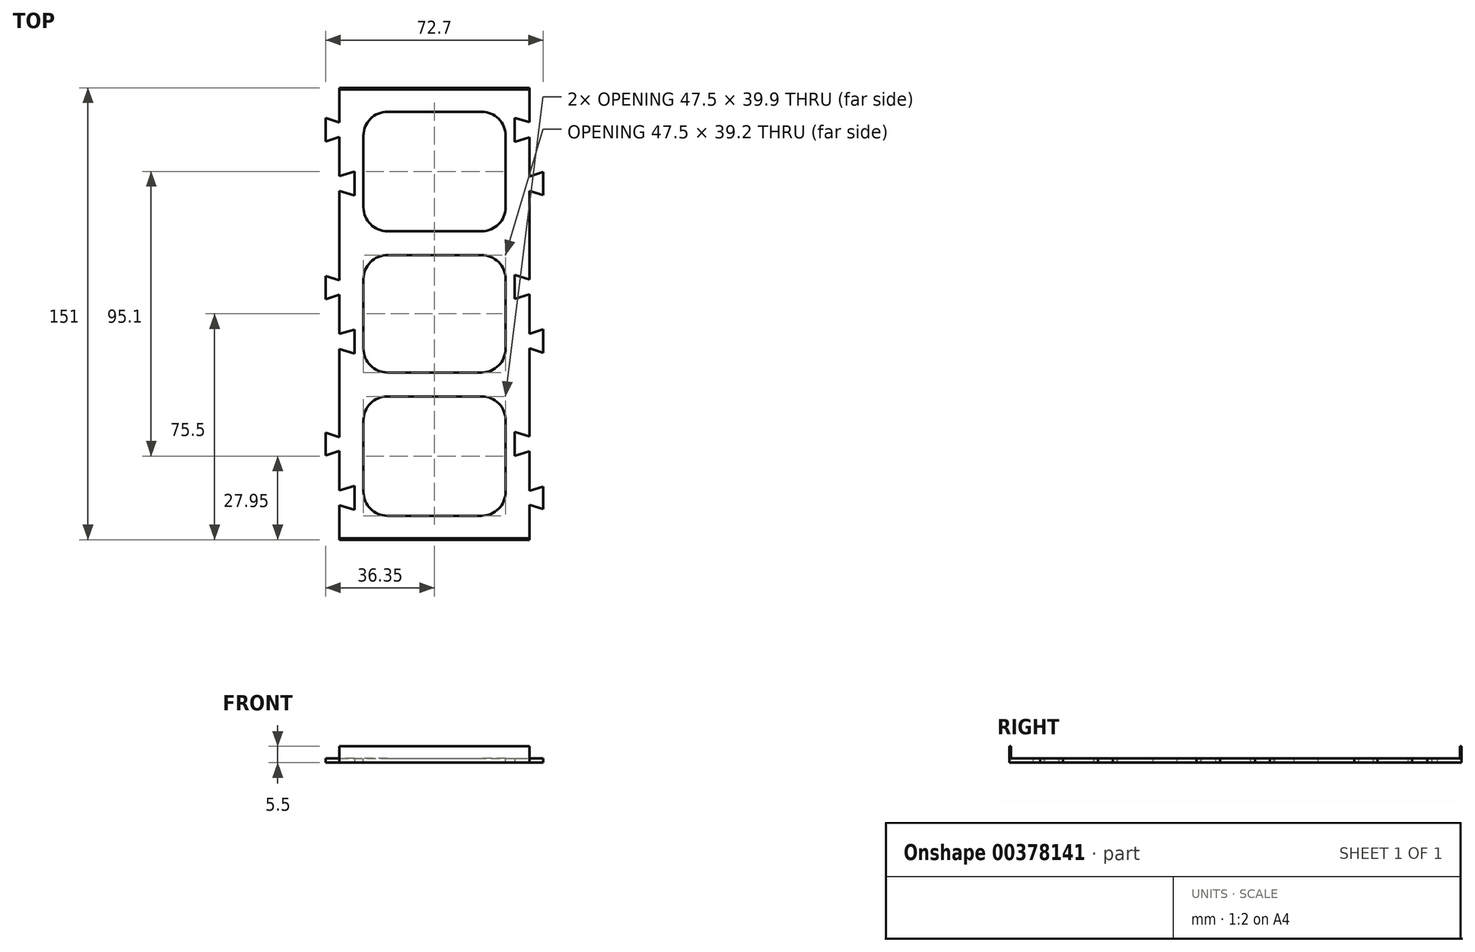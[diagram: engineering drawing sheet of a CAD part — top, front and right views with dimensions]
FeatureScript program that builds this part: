
annotation { "Feature Type Name" : "Feature", "Feature Type Description" : "" }
export const myFeature = defineFeature(function(context is Context, id is Id, definition is map)
    precondition{}
    {
        {
            var Q0;
            Q0=qCreatedBy(makeId("Top.planeOp"),FACE);
            var sketch = newSketch(context, id + "F0", { "sketchPlane" : qUnion([Q0])});
            skLineSegment(sketch, "E0", {"start": v(0, 0) * mm, "end": v(0, 11.5) * mm});
            skLineSegment(sketch, "E1", {"start": v(0, 11.5) * mm, "end": v(5, 10) * mm});
            skLineSegment(sketch, "E2", {"start": v(5, 10) * mm, "end": v(5, 18) * mm});
            skLineSegment(sketch, "E3", {"start": v(5, 18) * mm, "end": v(0, 16.5) * mm});
            skLineSegment(sketch, "E4", {"start": v(0, 16.5) * mm, "end": v(0, 29.7) * mm});
            skLineSegment(sketch, "E5", {"start": v(0, 29.7) * mm, "end": v(-4.6, 28.2) * mm});
            skLineSegment(sketch, "E6", {"start": v(-4.6, 28.2) * mm, "end": v(-4.6, 35.8) * mm});
            skLineSegment(sketch, "E7", {"start": v(-4.6, 35.8) * mm, "end": v(0, 34.3) * mm});
            skLineSegment(sketch, "E8", {"start": v(0, 34.3) * mm, "end": v(0, 63.75) * mm});
            skLineSegment(sketch, "E9", {"start": v(0, 63.75) * mm, "end": v(5, 62.25) * mm});
            skLineSegment(sketch, "E10", {"start": v(5, 62.25) * mm, "end": v(5, 70.25) * mm});
            skLineSegment(sketch, "E11", {"start": v(5, 70.25) * mm, "end": v(0, 68.75) * mm});
            skLineSegment(sketch, "E12", {"start": v(0, 68.75) * mm, "end": v(0, 81.85) * mm});
            skLineSegment(sketch, "E13", {"start": v(0, 81.85) * mm, "end": v(-4.6, 80.35) * mm});
            skLineSegment(sketch, "E14", {"start": v(-4.6, 80.35) * mm, "end": v(-4.6, 88.15) * mm});
            skLineSegment(sketch, "E15", {"start": v(-4.6, 88.15) * mm, "end": v(0, 86.65) * mm});
            skLineSegment(sketch, "E16", {"start": v(0, 86.65) * mm, "end": v(0, 116.5) * mm});
            skLineSegment(sketch, "E17", {"start": v(0, 116.5) * mm, "end": v(5, 115) * mm});
            skLineSegment(sketch, "E18", {"start": v(5, 115) * mm, "end": v(5, 123) * mm});
            skLineSegment(sketch, "E19", {"start": v(5, 123) * mm, "end": v(0, 121.5) * mm});
            skLineSegment(sketch, "E20", {"start": v(0, 121.5) * mm, "end": v(0, 134.6) * mm});
            skLineSegment(sketch, "E21", {"start": v(0, 134.6) * mm, "end": v(-4.6, 133.1) * mm});
            skLineSegment(sketch, "E22", {"start": v(-4.6, 133.1) * mm, "end": v(-4.6, 140.9) * mm});
            skLineSegment(sketch, "E23", {"start": v(-4.6, 140.9) * mm, "end": v(0, 139.4) * mm});
            skLineSegment(sketch, "E24", {"start": v(0, 139.4) * mm, "end": v(0, 151) * mm});
            skLineSegment(sketch, "E25", {"start": v(0, 151) * mm, "end": v(63.5, 151) * mm});
            skLineSegment(sketch, "E26", {"start": v(63.5, 151) * mm, "end": v(63.5, 139.5) * mm});
            skLineSegment(sketch, "E27", {"start": v(63.5, 139.5) * mm, "end": v(58.5, 141) * mm});
            skLineSegment(sketch, "E28", {"start": v(58.5, 141) * mm, "end": v(58.5, 133) * mm});
            skLineSegment(sketch, "E29", {"start": v(58.5, 133) * mm, "end": v(63.5, 134.5) * mm});
            skLineSegment(sketch, "E30", {"start": v(63.5, 134.5) * mm, "end": v(63.5, 121.4) * mm});
            skLineSegment(sketch, "E31", {"start": v(63.5, 121.4) * mm, "end": v(68.1, 122.9) * mm});
            skLineSegment(sketch, "E32", {"start": v(68.1, 122.9) * mm, "end": v(68.1, 115.1) * mm});
            skLineSegment(sketch, "E33", {"start": v(68.1, 115.1) * mm, "end": v(63.5, 116.6) * mm});
            skLineSegment(sketch, "E34", {"start": v(63.5, 116.6) * mm, "end": v(63.5, 87) * mm});
            skLineSegment(sketch, "E35", {"start": v(63.5, 87) * mm, "end": v(58.5, 88.5) * mm});
            skLineSegment(sketch, "E36", {"start": v(58.5, 88.5) * mm, "end": v(58.5, 80.5) * mm});
            skLineSegment(sketch, "E37", {"start": v(58.5, 80.5) * mm, "end": v(63.5, 82) * mm});
            skLineSegment(sketch, "E38", {"start": v(63.5, 82) * mm, "end": v(63.5, 68.8) * mm});
            skLineSegment(sketch, "E39", {"start": v(63.5, 68.8) * mm, "end": v(68.1, 70.3) * mm});
            skLineSegment(sketch, "E40", {"start": v(68.1, 70.3) * mm, "end": v(68.1, 62.5) * mm});
            skLineSegment(sketch, "E41", {"start": v(68.1, 62.5) * mm, "end": v(63.5, 64) * mm});
            skLineSegment(sketch, "E42", {"start": v(63.5, 64) * mm, "end": v(63.5, 34.5) * mm});
            skLineSegment(sketch, "E43", {"start": v(63.5, 34.5) * mm, "end": v(58.5, 36) * mm});
            skLineSegment(sketch, "E44", {"start": v(58.5, 36) * mm, "end": v(58.5, 28) * mm});
            skLineSegment(sketch, "E45", {"start": v(58.5, 28) * mm, "end": v(63.5, 29.5) * mm});
            skLineSegment(sketch, "E46", {"start": v(63.5, 29.5) * mm, "end": v(63.5, 16.3) * mm});
            skLineSegment(sketch, "E47", {"start": v(63.5, 16.3) * mm, "end": v(68.1, 17.8) * mm});
            skLineSegment(sketch, "E48", {"start": v(68.1, 17.8) * mm, "end": v(68.1, 10.2) * mm});
            skLineSegment(sketch, "E49", {"start": v(68.1, 10.2) * mm, "end": v(63.5, 11.7) * mm});
            skLineSegment(sketch, "E50", {"start": v(63.5, 11.7) * mm, "end": v(63.5, 0) * mm});
            skLineSegment(sketch, "E51", {"start": v(63.5, 0) * mm, "end": v(0, 0) * mm});
            skSolve(sketch);
        }
        {
            var Q0;
            Q0=makeQuery(id+"F0.imprint","IMPRINT",FACE,{"disambiguationData":[TD([[makeQuery(id+"F0.imprint","IMPRINT",EDGE,{"derivedFrom":sQuery(id+"F0.wireOp",EDGE,"E0")}),-1.0]])]});
            extrude(context, id + "F1", {"entities" : qUnion([Q0]), "depth" : 1.5 * mm});
        }
        {
            var Q0;
            Q0=makeQuery(id+"F1.opExtrude","CAP_FACE",FACE,{"disambiguationData":[OSD([sQuery(id+"F0.wireOp",EDGE,"E0"),sQuery(id+"F0.wireOp",EDGE,"E1"),sQuery(id+"F0.wireOp",EDGE,"E2"),sQuery(id+"F0.wireOp",EDGE,"E3"),sQuery(id+"F0.wireOp",EDGE,"E4"),sQuery(id+"F0.wireOp",EDGE,"E5"),sQuery(id+"F0.wireOp",EDGE,"E6"),sQuery(id+"F0.wireOp",EDGE,"E7"),sQuery(id+"F0.wireOp",EDGE,"E8"),sQuery(id+"F0.wireOp",EDGE,"E9"),sQuery(id+"F0.wireOp",EDGE,"E10"),sQuery(id+"F0.wireOp",EDGE,"E11"),sQuery(id+"F0.wireOp",EDGE,"E12"),sQuery(id+"F0.wireOp",EDGE,"E13"),sQuery(id+"F0.wireOp",EDGE,"E14"),sQuery(id+"F0.wireOp",EDGE,"E15"),sQuery(id+"F0.wireOp",EDGE,"E16"),sQuery(id+"F0.wireOp",EDGE,"E17"),sQuery(id+"F0.wireOp",EDGE,"E18"),sQuery(id+"F0.wireOp",EDGE,"E19"),sQuery(id+"F0.wireOp",EDGE,"E20"),sQuery(id+"F0.wireOp",EDGE,"E21"),sQuery(id+"F0.wireOp",EDGE,"E22"),sQuery(id+"F0.wireOp",EDGE,"E23"),sQuery(id+"F0.wireOp",EDGE,"E24"),sQuery(id+"F0.wireOp",EDGE,"E25"),sQuery(id+"F0.wireOp",EDGE,"E26"),sQuery(id+"F0.wireOp",EDGE,"E27"),sQuery(id+"F0.wireOp",EDGE,"E28"),sQuery(id+"F0.wireOp",EDGE,"E29"),sQuery(id+"F0.wireOp",EDGE,"E30"),sQuery(id+"F0.wireOp",EDGE,"E31"),sQuery(id+"F0.wireOp",EDGE,"E32"),sQuery(id+"F0.wireOp",EDGE,"E33"),sQuery(id+"F0.wireOp",EDGE,"E34"),sQuery(id+"F0.wireOp",EDGE,"E35"),sQuery(id+"F0.wireOp",EDGE,"E36"),sQuery(id+"F0.wireOp",EDGE,"E37"),sQuery(id+"F0.wireOp",EDGE,"E38"),sQuery(id+"F0.wireOp",EDGE,"E39"),sQuery(id+"F0.wireOp",EDGE,"E40"),sQuery(id+"F0.wireOp",EDGE,"E41"),sQuery(id+"F0.wireOp",EDGE,"E42"),sQuery(id+"F0.wireOp",EDGE,"E43"),sQuery(id+"F0.wireOp",EDGE,"E44"),sQuery(id+"F0.wireOp",EDGE,"E45"),sQuery(id+"F0.wireOp",EDGE,"E46"),sQuery(id+"F0.wireOp",EDGE,"E47"),sQuery(id+"F0.wireOp",EDGE,"E48"),sQuery(id+"F0.wireOp",EDGE,"E49"),sQuery(id+"F0.wireOp",EDGE,"E50"),sQuery(id+"F0.wireOp",EDGE,"E51")])],"isStart":false});
            var sketch = newSketch(context, id + "F2", { "sketchPlane" : qUnion([Q0])});
            skLineSegment(sketch, "E52.bottom", {"start": v(0, 151) * mm, "end": v(63.5, 151) * mm});
            skLineSegment(sketch, "E52.top", {"start": v(0, 150.5) * mm, "end": v(63.5, 150.5) * mm});
            skLineSegment(sketch, "E52.left", {"start": v(0, 151) * mm, "end": v(0, 150.5) * mm});
            skLineSegment(sketch, "E52.right", {"start": v(63.5, 151) * mm, "end": v(63.5, 150.5) * mm});
            skLineSegment(sketch, "E53.bottom", {"start": v(0, 0) * mm, "end": v(75.6, 0) * mm});
            skLineSegment(sketch, "E53.top", {"start": v(0, 0.5) * mm, "end": v(75.6, 0.5) * mm});
            skLineSegment(sketch, "E53.left", {"start": v(0, 0) * mm, "end": v(0, 0.5) * mm});
            skLineSegment(sketch, "E53.right", {"start": v(75.6, 0) * mm, "end": v(75.6, 0.5) * mm});
            skSolve(sketch);
        }
        {
            var Q0;
            Q0=makeQuery(id+"F2.imprint","IMPRINT",FACE,{"disambiguationData":[TD([[makeQuery(id+"F2.imprint","IMPRINT",EDGE,{"derivedFrom":sQuery(id+"F2.wireOp",EDGE,"E53.bottom")}),-1.0]])]});
            var Q1;
            Q1=makeQuery(id+"F2.imprint","IMPRINT",FACE,{"disambiguationData":[TD([[makeQuery(id+"F2.imprint","IMPRINT",EDGE,{"derivedFrom":sQuery(id+"F2.wireOp",EDGE,"E52.bottom")}),-1.0]])]});
            extrude(context, id + "F3", {"entities" : qUnion([Q0, Q1]), "operationType" : NewBodyOperationType.ADD, "depth" : 4 * mm});
        }
        {
            var Q0;
            Q0=makeQuery(id+"F1.opExtrude","CAP_FACE",FACE,{"disambiguationData":[OSD([sQuery(id+"F0.wireOp",EDGE,"E0"),sQuery(id+"F0.wireOp",EDGE,"E1"),sQuery(id+"F0.wireOp",EDGE,"E2"),sQuery(id+"F0.wireOp",EDGE,"E3"),sQuery(id+"F0.wireOp",EDGE,"E4"),sQuery(id+"F0.wireOp",EDGE,"E5"),sQuery(id+"F0.wireOp",EDGE,"E6"),sQuery(id+"F0.wireOp",EDGE,"E7"),sQuery(id+"F0.wireOp",EDGE,"E8"),sQuery(id+"F0.wireOp",EDGE,"E9"),sQuery(id+"F0.wireOp",EDGE,"E10"),sQuery(id+"F0.wireOp",EDGE,"E11"),sQuery(id+"F0.wireOp",EDGE,"E12"),sQuery(id+"F0.wireOp",EDGE,"E13"),sQuery(id+"F0.wireOp",EDGE,"E14"),sQuery(id+"F0.wireOp",EDGE,"E15"),sQuery(id+"F0.wireOp",EDGE,"E16"),sQuery(id+"F0.wireOp",EDGE,"E17"),sQuery(id+"F0.wireOp",EDGE,"E18"),sQuery(id+"F0.wireOp",EDGE,"E19"),sQuery(id+"F0.wireOp",EDGE,"E20"),sQuery(id+"F0.wireOp",EDGE,"E21"),sQuery(id+"F0.wireOp",EDGE,"E22"),sQuery(id+"F0.wireOp",EDGE,"E23"),sQuery(id+"F0.wireOp",EDGE,"E24"),sQuery(id+"F0.wireOp",EDGE,"E25"),sQuery(id+"F0.wireOp",EDGE,"E26"),sQuery(id+"F0.wireOp",EDGE,"E27"),sQuery(id+"F0.wireOp",EDGE,"E28"),sQuery(id+"F0.wireOp",EDGE,"E29"),sQuery(id+"F0.wireOp",EDGE,"E30"),sQuery(id+"F0.wireOp",EDGE,"E31"),sQuery(id+"F0.wireOp",EDGE,"E32"),sQuery(id+"F0.wireOp",EDGE,"E33"),sQuery(id+"F0.wireOp",EDGE,"E34"),sQuery(id+"F0.wireOp",EDGE,"E35"),sQuery(id+"F0.wireOp",EDGE,"E36"),sQuery(id+"F0.wireOp",EDGE,"E37"),sQuery(id+"F0.wireOp",EDGE,"E38"),sQuery(id+"F0.wireOp",EDGE,"E39"),sQuery(id+"F0.wireOp",EDGE,"E40"),sQuery(id+"F0.wireOp",EDGE,"E41"),sQuery(id+"F0.wireOp",EDGE,"E42"),sQuery(id+"F0.wireOp",EDGE,"E43"),sQuery(id+"F0.wireOp",EDGE,"E44"),sQuery(id+"F0.wireOp",EDGE,"E45"),sQuery(id+"F0.wireOp",EDGE,"E46"),sQuery(id+"F0.wireOp",EDGE,"E47"),sQuery(id+"F0.wireOp",EDGE,"E48"),sQuery(id+"F0.wireOp",EDGE,"E49"),sQuery(id+"F0.wireOp",EDGE,"E50"),sQuery(id+"F0.wireOp",EDGE,"E51")])],"isStart":false});
            var sketch = newSketch(context, id + "F4", { "sketchPlane" : qUnion([Q0])});
            skLineSegment(sketch, "E54.bottom", {"start": v(8, 47.9) * mm, "end": v(55.5, 47.9) * mm});
            skLineSegment(sketch, "E54.top", {"start": v(8, 8) * mm, "end": v(55.5, 8) * mm});
            skLineSegment(sketch, "E54.left", {"start": v(8, 47.9) * mm, "end": v(8, 8) * mm});
            skLineSegment(sketch, "E54.right", {"start": v(55.5, 47.9) * mm, "end": v(55.5, 8) * mm});
            skLineSegment(sketch, "E55.bottom", {"start": v(8, 95.1) * mm, "end": v(55.5, 95.1) * mm});
            skLineSegment(sketch, "E55.top", {"start": v(8, 55.9) * mm, "end": v(55.5, 55.9) * mm});
            skLineSegment(sketch, "E55.left", {"start": v(8, 95.1) * mm, "end": v(8, 55.9) * mm});
            skLineSegment(sketch, "E55.right", {"start": v(55.5, 95.1) * mm, "end": v(55.5, 55.9) * mm});
            skLineSegment(sketch, "E56.bottom", {"start": v(8, 143) * mm, "end": v(55.5, 143) * mm});
            skLineSegment(sketch, "E56.top", {"start": v(8, 103.1) * mm, "end": v(55.5, 103.1) * mm});
            skLineSegment(sketch, "E56.left", {"start": v(8, 143) * mm, "end": v(8, 103.1) * mm});
            skLineSegment(sketch, "E56.right", {"start": v(55.5, 143) * mm, "end": v(55.5, 103.1) * mm});
            skSolve(sketch);
        }
        {
            var Q0;
            Q0=makeQuery(id+"F4.imprint","IMPRINT",FACE,{"disambiguationData":[TD([[makeQuery(id+"F4.imprint","IMPRINT",EDGE,{"derivedFrom":sQuery(id+"F4.wireOp",EDGE,"E56.bottom")}),-1.0]])]});
            var Q1;
            Q1=makeQuery(id+"F4.imprint","IMPRINT",FACE,{"disambiguationData":[TD([[makeQuery(id+"F4.imprint","IMPRINT",EDGE,{"derivedFrom":sQuery(id+"F4.wireOp",EDGE,"E55.bottom")}),-1.0]])]});
            var Q2;
            Q2=makeQuery(id+"F4.imprint","IMPRINT",FACE,{"disambiguationData":[TD([[makeQuery(id+"F4.imprint","IMPRINT",EDGE,{"derivedFrom":sQuery(id+"F4.wireOp",EDGE,"E54.bottom")}),-1.0]])]});
            extrude(context, id + "F5", {"entities" : qUnion([Q0, Q1, Q2]), "operationType" : NewBodyOperationType.REMOVE, "endBound" : BoundingType.THROUGH_ALL, "oppositeDirection" : true, "depth" : 25 * mm});
        }
        {
            var Q0;
            Q0=makeQuery(id+"F5.boolean.opBoolean","COPY",EDGE,{"derivedFrom":makeQuery(id+"F5.opExtrude","SWEPT_EDGE",EDGE,{"disambiguationData":[OSD([sQuery(id+"F4.wireOp",EDGE,"E56.bottom"),sQuery(id+"F4.wireOp",EDGE,"E56.left")])]})});
            var Q1;
            Q1=makeQuery(id+"F5.boolean.opBoolean","COPY",EDGE,{"derivedFrom":makeQuery(id+"F5.opExtrude","SWEPT_EDGE",EDGE,{"disambiguationData":[OSD([sQuery(id+"F4.wireOp",EDGE,"E55.bottom"),sQuery(id+"F4.wireOp",EDGE,"E55.left")])]})});
            var Q2;
            Q2=makeQuery(id+"F5.boolean.opBoolean","COPY",EDGE,{"derivedFrom":makeQuery(id+"F5.opExtrude","SWEPT_EDGE",EDGE,{"disambiguationData":[OSD([sQuery(id+"F4.wireOp",EDGE,"E54.bottom"),sQuery(id+"F4.wireOp",EDGE,"E54.left")])]})});
            var Q3;
            Q3=makeQuery(id+"F5.boolean.opBoolean","COPY",EDGE,{"derivedFrom":makeQuery(id+"F5.opExtrude","SWEPT_EDGE",EDGE,{"disambiguationData":[OSD([sQuery(id+"F4.wireOp",EDGE,"E56.top"),sQuery(id+"F4.wireOp",EDGE,"E56.left")])]})});
            var Q4;
            Q4=makeQuery(id+"F5.boolean.opBoolean","COPY",EDGE,{"derivedFrom":makeQuery(id+"F5.opExtrude","SWEPT_EDGE",EDGE,{"disambiguationData":[OSD([sQuery(id+"F4.wireOp",EDGE,"E55.top"),sQuery(id+"F4.wireOp",EDGE,"E55.left")])]})});
            var Q5;
            Q5=makeQuery(id+"F5.boolean.opBoolean","COPY",EDGE,{"derivedFrom":makeQuery(id+"F5.opExtrude","SWEPT_EDGE",EDGE,{"disambiguationData":[OSD([sQuery(id+"F4.wireOp",EDGE,"E54.top"),sQuery(id+"F4.wireOp",EDGE,"E54.left")])]})});
            var Q6;
            Q6=makeQuery(id+"F5.boolean.opBoolean","COPY",EDGE,{"derivedFrom":makeQuery(id+"F5.opExtrude","SWEPT_EDGE",EDGE,{"disambiguationData":[OSD([sQuery(id+"F4.wireOp",EDGE,"E54.top"),sQuery(id+"F4.wireOp",EDGE,"E54.right")])]})});
            var Q7;
            Q7=makeQuery(id+"F5.boolean.opBoolean","COPY",EDGE,{"derivedFrom":makeQuery(id+"F5.opExtrude","SWEPT_EDGE",EDGE,{"disambiguationData":[OSD([sQuery(id+"F4.wireOp",EDGE,"E55.top"),sQuery(id+"F4.wireOp",EDGE,"E55.right")])]})});
            var Q8;
            Q8=makeQuery(id+"F5.boolean.opBoolean","COPY",EDGE,{"derivedFrom":makeQuery(id+"F5.opExtrude","SWEPT_EDGE",EDGE,{"disambiguationData":[OSD([sQuery(id+"F4.wireOp",EDGE,"E56.top"),sQuery(id+"F4.wireOp",EDGE,"E56.right")])]})});
            var Q9;
            Q9=makeQuery(id+"F5.boolean.opBoolean","COPY",EDGE,{"derivedFrom":makeQuery(id+"F5.opExtrude","SWEPT_EDGE",EDGE,{"disambiguationData":[OSD([sQuery(id+"F4.wireOp",EDGE,"E56.bottom"),sQuery(id+"F4.wireOp",EDGE,"E56.right")])]})});
            var Q10;
            Q10=makeQuery(id+"F5.boolean.opBoolean","COPY",EDGE,{"derivedFrom":makeQuery(id+"F5.opExtrude","SWEPT_EDGE",EDGE,{"disambiguationData":[OSD([sQuery(id+"F4.wireOp",EDGE,"E55.bottom"),sQuery(id+"F4.wireOp",EDGE,"E55.right")])]})});
            var Q11;
            Q11=makeQuery(id+"F5.boolean.opBoolean","COPY",EDGE,{"derivedFrom":makeQuery(id+"F5.opExtrude","SWEPT_EDGE",EDGE,{"disambiguationData":[OSD([sQuery(id+"F4.wireOp",EDGE,"E54.bottom"),sQuery(id+"F4.wireOp",EDGE,"E54.right")])]})});
            fillet(context, id + "F6", {"entities" : qUnion([Q0, Q1, Q2, Q3, Q4, Q5, Q6, Q7, Q8, Q9, Q10, Q11]), "radius" : 8 * mm, "tangentPropagation" : true, "allowEdgeOverflow" : false});
        }
    });
